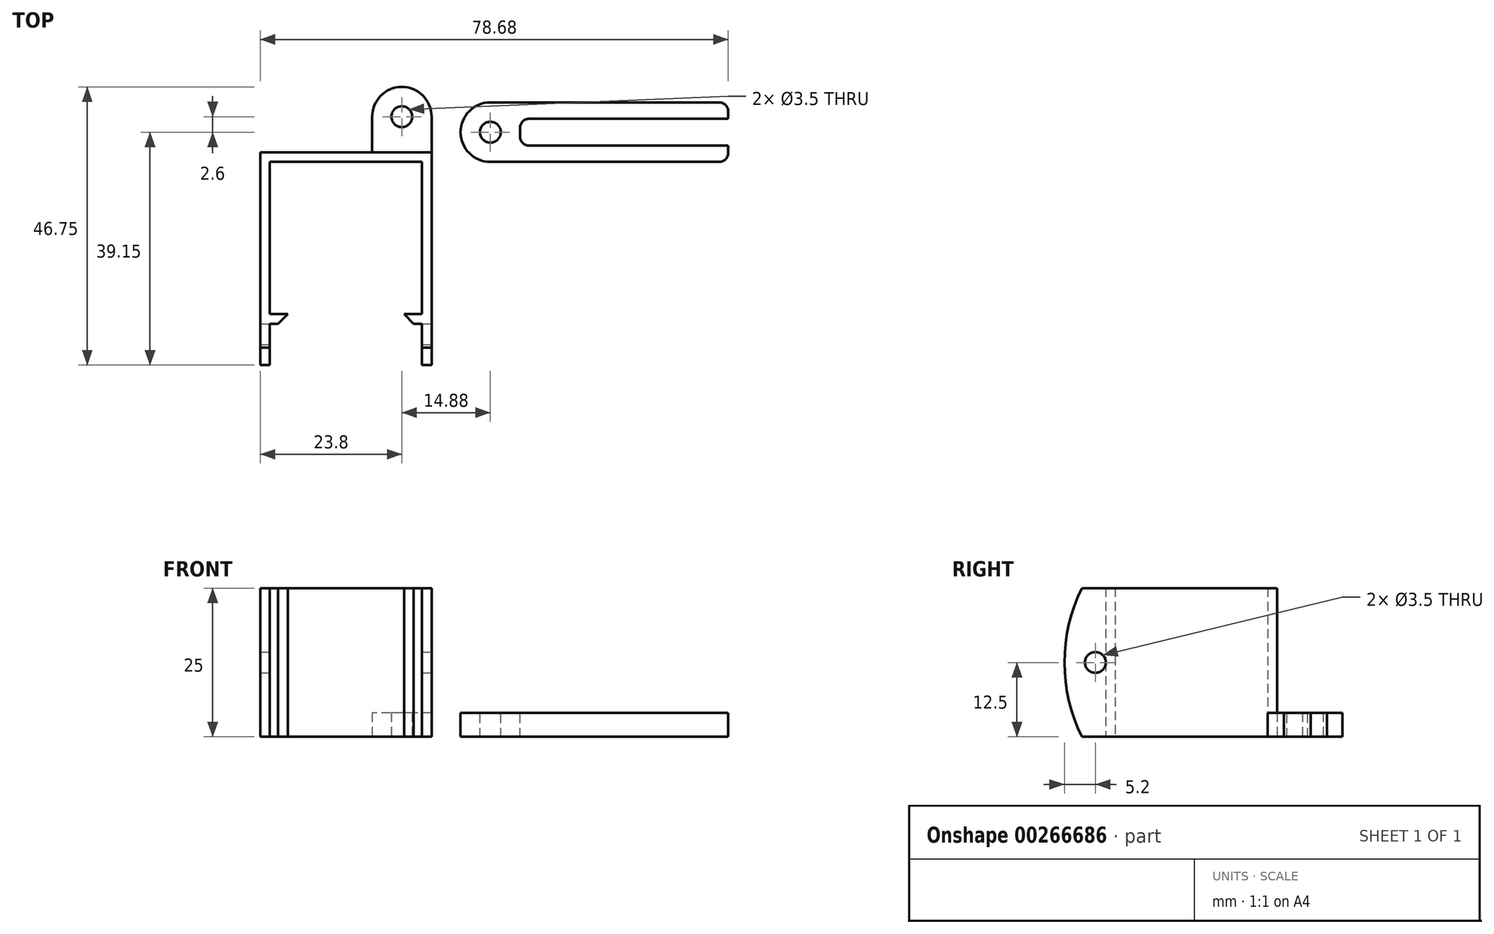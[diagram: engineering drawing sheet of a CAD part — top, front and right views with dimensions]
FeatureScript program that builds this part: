
annotation { "Feature Type Name" : "Feature", "Feature Type Description" : "" }
export const myFeature = defineFeature(function(context is Context, id is Id, definition is map)
    precondition{}
    {
        {
            var Q0;
            Q0=qCreatedBy(makeId("Top.planeOp"),FACE);
            var sketch = newSketch(context, id + "F0", { "sketchPlane" : qUnion([Q0])});
            skLineSegment(sketch, "E0", {"start": v(0, 0) * mm, "end": v(0, -25.6) * mm});
            skLineSegment(sketch, "E1", {"start": v(0, -25.6) * mm, "end": v(-3, -25.6) * mm});
            skLineSegment(sketch, "E2", {"start": v(-3, -25.6) * mm, "end": v(-3, -27.2) * mm});
            skLineSegment(sketch, "E3", {"start": v(-3, -27.2) * mm, "end": v(0, -27.2) * mm});
            skLineSegment(sketch, "E4", {"start": v(0, -27.2) * mm, "end": v(0, -31.2) * mm});
            skLineSegment(sketch, "E5", {"start": v(0, -31.2) * mm, "end": v(1.6, -31.2) * mm});
            skLineSegment(sketch, "E6", {"start": v(1.6, -31.2) * mm, "end": v(1.6, 1.6) * mm});
            skLineSegment(sketch, "E7", {"start": v(1.6, 1.6) * mm, "end": v(-27.2, 1.6) * mm});
            skLineSegment(sketch, "E8", {"start": v(-27.2, 1.6) * mm, "end": v(-27.2, -31.2) * mm});
            skLineSegment(sketch, "E9", {"start": v(-27.2, -31.2) * mm, "end": v(-25.6, -31.2) * mm});
            skLineSegment(sketch, "E10", {"start": v(-25.6, -31.2) * mm, "end": v(-25.6, -27.2) * mm});
            skLineSegment(sketch, "E11", {"start": v(-25.6, -27.2) * mm, "end": v(-22.6, -27.2) * mm});
            skLineSegment(sketch, "E12", {"start": v(-22.6, -27.2) * mm, "end": v(-22.6, -25.6) * mm});
            skLineSegment(sketch, "E13", {"start": v(-22.6, -25.6) * mm, "end": v(-25.6, -25.6) * mm});
            skLineSegment(sketch, "E14", {"start": v(-25.6, -25.6) * mm, "end": v(-25.6, 0) * mm});
            skLineSegment(sketch, "E15", {"start": v(-25.6, 0) * mm, "end": v(0, 0) * mm});
            skSolve(sketch);
        }
        {
            var Q0;
            Q0=qSketchRegion(id+"F0",true);
            extrude(context, id + "F1", {"entities" : qUnion([Q0]), "depth" : 25 * mm});
        }
        {
            var Q0;
            Q0=makeQuery(id+"F1.opExtrude","SWEPT_EDGE",EDGE,{"disambiguationData":[OSD([sQuery(id+"F0.wireOp",EDGE,"E11"),sQuery(id+"F0.wireOp",EDGE,"E12")])]});
            var Q1;
            Q1=makeQuery(id+"F1.opExtrude","SWEPT_EDGE",EDGE,{"disambiguationData":[OSD([sQuery(id+"F0.wireOp",EDGE,"E2"),sQuery(id+"F0.wireOp",EDGE,"E3")])]});
            chamfer(context, id + "F2", {"entities" : qUnion([Q0, Q1]), "width" : 1.6 * mm, "tangentPropagation" : true});
        }
        {
            var Q0;
            Q0=makeQuery(id+"F1.opExtrude","SWEPT_FACE",FACE,{"disambiguationData":[OSD([sQuery(id+"F0.wireOp",EDGE,"E8")])]});
            var sketch = newSketch(context, id + "F3", { "sketchPlane" : qUnion([Q0])});
            skArc(sketch, "E16", {"start": v(31.2, 0) * mm, "mid": v(34.15, 12.5) * mm, "end": v(31.2, 25) * mm});
            skLineSegment(sketch, "E17", {"start": v(31.2, 25) * mm, "end": v(31.2, 0) * mm});
            skSolve(sketch);
        }
        {
            var Q0;
            Q0=qSketchRegion(id+"F3",true);
            var Q1;
            Q1=makeQuery(id+"F1.opExtrude","SWEPT_FACE",FACE,{"disambiguationData":[OSD([sQuery(id+"F0.wireOp",EDGE,"E10")])]});
            extrude(context, id + "F4", {"entities" : qUnion([Q0]), "operationType" : NewBodyOperationType.ADD, "endBound" : BoundingType.UP_TO_SURFACE, "oppositeDirection" : true, "endBoundEntityFace" : qUnion([Q1]), "depth" : 25 * mm});
        }
        {
            var Q0;
            Q0=makeQuery(id+"F1.opExtrude","SWEPT_FACE",FACE,{"disambiguationData":[OSD([sQuery(id+"F0.wireOp",EDGE,"E6")])]});
            var sketch = newSketch(context, id + "F5", { "sketchPlane" : qUnion([Q0])});
            skArc(sketch, "E18", {"start": v(-31.2, 25) * mm, "mid": v(-34.15, 12.5) * mm, "end": v(-31.2, 0) * mm});
            skLineSegment(sketch, "E19", {"start": v(-31.2, 25) * mm, "end": v(-31.2, 0) * mm});
            skSolve(sketch);
        }
        {
            var Q0;
            Q0=qSketchRegion(id+"F5",true);
            var Q1;
            Q1=makeQuery(id+"F1.opExtrude","SWEPT_FACE",FACE,{"disambiguationData":[OSD([sQuery(id+"F0.wireOp",EDGE,"E4")])]});
            extrude(context, id + "F6", {"entities" : qUnion([Q0]), "operationType" : NewBodyOperationType.ADD, "endBound" : BoundingType.UP_TO_SURFACE, "oppositeDirection" : true, "endBoundEntityFace" : qUnion([Q1]), "depth" : 25 * mm});
        }
        {
            var Q0;
            Q0=makeQuery(id+"F4.boolean.opBoolean","MERGE",FACE,{"derivedFrom":[makeQuery(id+"F1.opExtrude","SWEPT_FACE",FACE,{"disambiguationData":[OSD([sQuery(id+"F0.wireOp",EDGE,"E10")])]}),makeQuery(id+"F4.opExtrude","CAP_FACE",FACE,{"disambiguationData":[OSD([sQuery(id+"F3.wireOp",EDGE,"E16"),sQuery(id+"F3.wireOp",EDGE,"E17")])],"isStart":false})]});
            var sketch = newSketch(context, id + "F7", { "sketchPlane" : qUnion([Q0])});
            skCircle(sketch, "E20", {"center": v(-28.95, 12.5) * mm, "radius": 1.75 * mm});
            skPoint(sketch, "E21", {"position": v(-27.2, 12.5) * mm});
            skSolve(sketch);
        }
        {
            var Q0;
            Q0=qSketchRegion(id+"F7",true);
            extrude(context, id + "F8", {"entities" : qUnion([Q0]), "operationType" : NewBodyOperationType.REMOVE, "oppositeDirection" : true, "depth" : 100 * mm, "symmetric" : true});
        }
        {
            var Q0;
            Q0=qCreatedBy(makeId("Top.planeOp"),FACE);
            var sketch = newSketch(context, id + "F9", { "sketchPlane" : qUnion([Q0])});
            skCircle(sketch, "E22", {"center": v(-3.4, 7.6) * mm, "radius": 5 * mm});
            skLineSegment(sketch, "E23", {"start": v(1.6, 7.6) * mm, "end": v(1.6, 1.6) * mm});
            skLineSegment(sketch, "E24", {"start": v(1.6, 1.6) * mm, "end": v(-8.4, 1.6) * mm});
            skLineSegment(sketch, "E25", {"start": v(-8.4, 1.6) * mm, "end": v(-8.4, 7.6) * mm});
            skSolve(sketch);
        }
        {
            var Q0;
            Q0=qSketchRegion(id+"F9",true);
            extrude(context, id + "F10", {"entities" : qUnion([Q0]), "operationType" : NewBodyOperationType.ADD, "depth" : 4 * mm});
        }
        {
            var Q0;
            Q0=qCreatedBy(makeId("Top.planeOp"),FACE);
            var sketch = newSketch(context, id + "F11", { "sketchPlane" : qUnion([Q0])});
            skCircle(sketch, "E26", {"center": v(-3.4, 7.6) * mm, "radius": 1.75 * mm});
            skSolve(sketch);
        }
        {
            var Q0;
            Q0=qSketchRegion(id+"F11",true);
            extrude(context, id + "F12", {"entities" : qUnion([Q0]), "operationType" : NewBodyOperationType.REMOVE, "endBound" : BoundingType.THROUGH_ALL, "depth" : 25 * mm});
        }
        {
            var Q0;
            Q0=qCreatedBy(makeId("Top.planeOp"),FACE);
            var sketch = newSketch(context, id + "F13", { "sketchPlane" : qUnion([Q0])});
            skLineSegment(sketch, "E27.bottom", {"start": v(6.48, 0) * mm, "end": v(51.48, 0) * mm});
            skLineSegment(sketch, "E27.top", {"start": v(6.48, 10) * mm, "end": v(51.48, 10) * mm});
            skLineSegment(sketch, "E27.left", {"start": v(6.48, 0) * mm, "end": v(6.48, 10) * mm});
            skLineSegment(sketch, "E27.right", {"start": v(51.48, 0) * mm, "end": v(51.48, 10) * mm});
            skSolve(sketch);
        }
        {
            var Q0;
            Q0=qSketchRegion(id+"F13",true);
            extrude(context, id + "F14", {"entities" : qUnion([Q0]), "depth" : 4 * mm});
        }
        {
            var Q0;
            Q0=makeQuery(id+"F14.opExtrude","SWEPT_EDGE",EDGE,{"disambiguationData":[OSD([sQuery(id+"F13.wireOp",EDGE,"E27.bottom"),sQuery(id+"F13.wireOp",EDGE,"E27.left")])]});
            var Q1;
            Q1=makeQuery(id+"F14.opExtrude","SWEPT_EDGE",EDGE,{"disambiguationData":[OSD([sQuery(id+"F13.wireOp",EDGE,"E27.top"),sQuery(id+"F13.wireOp",EDGE,"E27.left")])]});
            fillet(context, id + "F15", {"entities" : qUnion([Q0, Q1]), "radius" : 5 * mm, "tangentPropagation" : true, "allowEdgeOverflow" : false});
        }
        {
            var Q0;
            Q0=makeQuery(id+"F14.opExtrude","CAP_FACE",FACE,{"disambiguationData":[OSD([sQuery(id+"F13.wireOp",EDGE,"E27.bottom"),sQuery(id+"F13.wireOp",EDGE,"E27.top"),sQuery(id+"F13.wireOp",EDGE,"E27.left"),sQuery(id+"F13.wireOp",EDGE,"E27.right")])],"isStart":false});
            var sketch = newSketch(context, id + "F16", { "sketchPlane" : qUnion([Q0])});
            skCircle(sketch, "E28", {"center": v(11.48, 5) * mm, "radius": 1.75 * mm});
            skSolve(sketch);
        }
        {
            var Q0;
            Q0=qSketchRegion(id+"F16",true);
            extrude(context, id + "F17", {"entities" : qUnion([Q0]), "operationType" : NewBodyOperationType.REMOVE, "endBound" : BoundingType.THROUGH_ALL, "oppositeDirection" : true, "depth" : 25 * mm});
        }
        {
            var Q0;
            Q0=makeQuery(id+"F14.opExtrude","CAP_FACE",FACE,{"disambiguationData":[OSD([sQuery(id+"F13.wireOp",EDGE,"E27.bottom"),sQuery(id+"F13.wireOp",EDGE,"E27.top"),sQuery(id+"F13.wireOp",EDGE,"E27.left"),sQuery(id+"F13.wireOp",EDGE,"E27.right")])],"isStart":false});
            var sketch = newSketch(context, id + "F18", { "sketchPlane" : qUnion([Q0])});
            skLineSegment(sketch, "E29.bottom", {"start": v(51.48, 7.25) * mm, "end": v(16.48, 7.25) * mm});
            skLineSegment(sketch, "E29.top", {"start": v(51.48, 2.75) * mm, "end": v(16.48, 2.75) * mm});
            skLineSegment(sketch, "E29.left", {"start": v(51.48, 7.25) * mm, "end": v(51.48, 2.75) * mm});
            skLineSegment(sketch, "E29.right", {"start": v(16.48, 7.25) * mm, "end": v(16.48, 2.75) * mm});
            skPoint(sketch, "E30", {"position": v(51.48, 5) * mm});
            skSolve(sketch);
        }
        {
            var Q0;
            Q0=qSketchRegion(id+"F18",true);
            extrude(context, id + "F19", {"entities" : qUnion([Q0]), "operationType" : NewBodyOperationType.REMOVE, "endBound" : BoundingType.THROUGH_ALL, "oppositeDirection" : true, "depth" : 25 * mm});
        }
        {
            var Q0;
            Q0=makeQuery(id+"F19.boolean.opBoolean","COPY",EDGE,{"derivedFrom":makeQuery(id+"F19.opExtrude","SWEPT_EDGE",EDGE,{"disambiguationData":[OSD([sQuery(id+"F18.wireOp",EDGE,"E29.bottom"),sQuery(id+"F18.wireOp",EDGE,"E29.right")])]})});
            var Q1;
            Q1=makeQuery(id+"F19.boolean.opBoolean","COPY",EDGE,{"derivedFrom":makeQuery(id+"F19.opExtrude","SWEPT_EDGE",EDGE,{"disambiguationData":[OSD([sQuery(id+"F13.wireOp",EDGE,"E27.right"),sQuery(id+"F18.wireOp",EDGE,"E29.bottom"),sQuery(id+"F18.wireOp",EDGE,"E29.left")])]})});
            var Q2;
            Q2=makeQuery(id+"F14.opExtrude","SWEPT_EDGE",EDGE,{"disambiguationData":[OSD([sQuery(id+"F13.wireOp",EDGE,"E27.top"),sQuery(id+"F13.wireOp",EDGE,"E27.right")])]});
            var Q3;
            Q3=makeQuery(id+"F19.boolean.opBoolean","COPY",EDGE,{"derivedFrom":makeQuery(id+"F19.opExtrude","SWEPT_EDGE",EDGE,{"disambiguationData":[OSD([sQuery(id+"F13.wireOp",EDGE,"E27.right"),sQuery(id+"F18.wireOp",EDGE,"E29.top"),sQuery(id+"F18.wireOp",EDGE,"E29.left")])]})});
            var Q4;
            Q4=makeQuery(id+"F14.opExtrude","SWEPT_EDGE",EDGE,{"disambiguationData":[OSD([sQuery(id+"F13.wireOp",EDGE,"E27.bottom"),sQuery(id+"F13.wireOp",EDGE,"E27.right")])]});
            var Q5;
            Q5=makeQuery(id+"F19.boolean.opBoolean","COPY",EDGE,{"derivedFrom":makeQuery(id+"F19.opExtrude","SWEPT_EDGE",EDGE,{"disambiguationData":[OSD([sQuery(id+"F18.wireOp",EDGE,"E29.top"),sQuery(id+"F18.wireOp",EDGE,"E29.right")])]})});
            fillet(context, id + "F20", {"entities" : qUnion([Q0, Q1, Q2, Q3, Q4, Q5]), "radius" : 1.5 * mm, "tangentPropagation" : true, "allowEdgeOverflow" : false});
        }
    });
